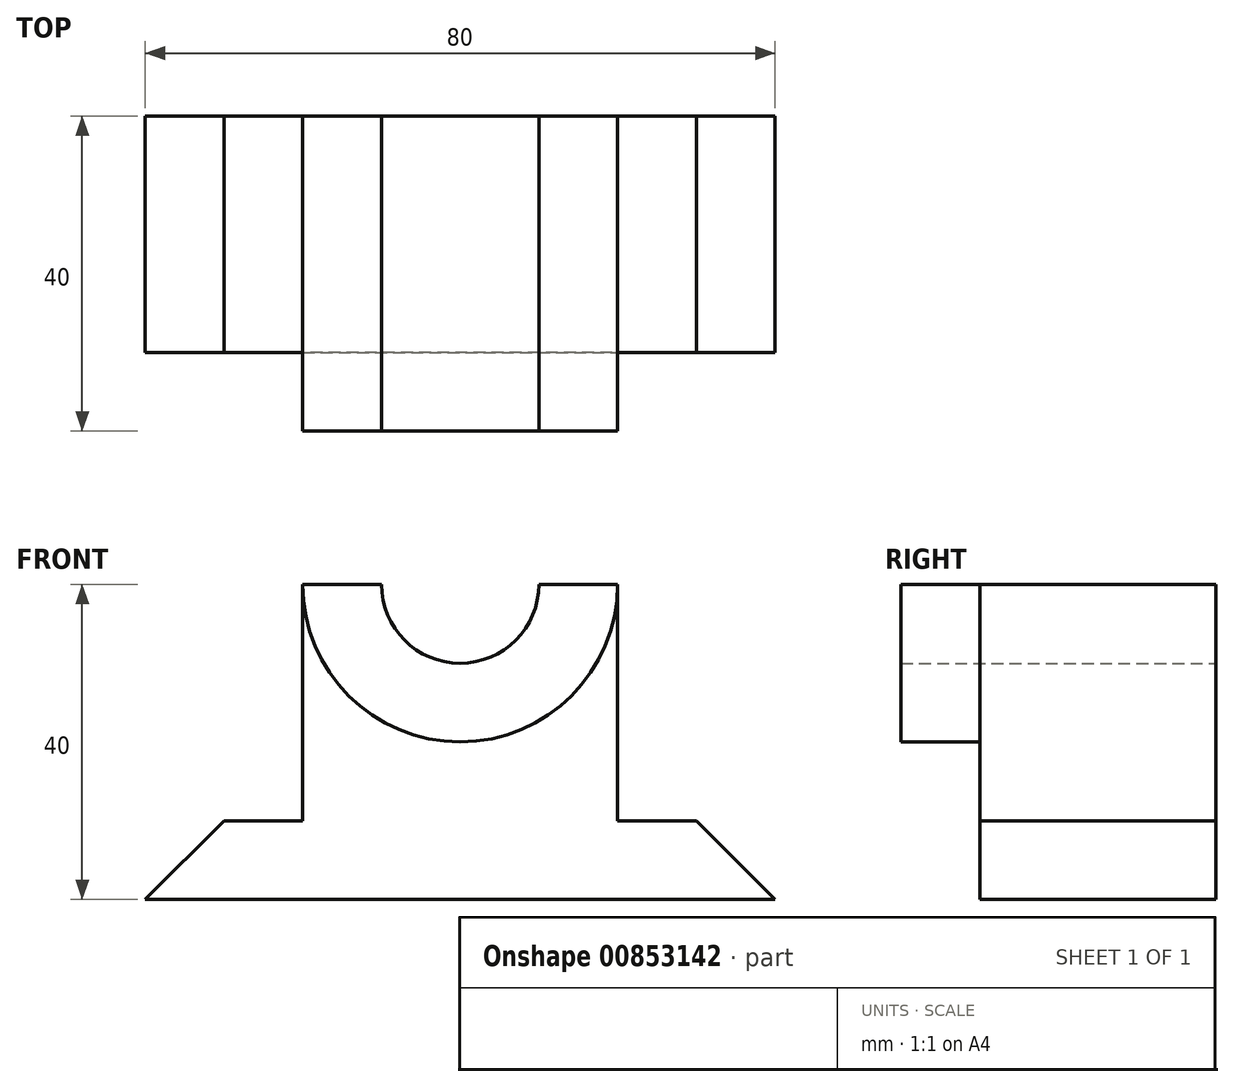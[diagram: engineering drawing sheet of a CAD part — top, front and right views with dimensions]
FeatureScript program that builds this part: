
annotation { "Feature Type Name" : "Feature", "Feature Type Description" : "" }
export const myFeature = defineFeature(function(context is Context, id is Id, definition is map)
    precondition{}
    {
        {
            var Q0;
            Q0=qCreatedBy(makeId("Front.planeOp"),FACE);
            var sketch = newSketch(context, id + "F0", { "sketchPlane" : qUnion([Q0])});
            skLineSegment(sketch, "E0", {"start": v(-40, 0) * mm, "end": v(-30, 10) * mm});
            skLineSegment(sketch, "E1", {"start": v(-30, 10) * mm, "end": v(-20, 10) * mm});
            skLineSegment(sketch, "E2", {"start": v(-20, 10) * mm, "end": v(-20, 40) * mm});
            skLineSegment(sketch, "E3", {"start": v(-20, 40) * mm, "end": v(-10, 40) * mm});
            skLineSegment(sketch, "E4", {"start": v(20, 40) * mm, "end": v(20, 10) * mm});
            skLineSegment(sketch, "E5", {"start": v(20, 10) * mm, "end": v(30, 10) * mm});
            skLineSegment(sketch, "E6", {"start": v(30, 10) * mm, "end": v(40, 0) * mm});
            skLineSegment(sketch, "E7", {"start": v(40, 0) * mm, "end": v(-40, 0) * mm});
            skArc(sketch, "E8", {"start": v(-10, 40) * mm, "mid": v(0, 30) * mm, "end": v(10, 40) * mm});
            skLineSegment(sketch, "E9.trimOffspring", {"start": v(10, 40) * mm, "end": v(20, 40) * mm});
            skSolve(sketch);
        }
        {
            var Q0;
            Q0 = qSketchRegion(id + "F0", true);
            extrude(context, id + "F1", {"entities" : qUnion([Q0]), "depth" : 30 * mm, "offsetDistance" : 25 * mm});
        }
        {
            var Q0;
            Q0=makeQuery(id+"F1.opExtrude","CAP_FACE",FACE,{"disambiguationData":[OSD([sQuery(id+"F0.wireOp",EDGE,"E0"),sQuery(id+"F0.wireOp",EDGE,"E1"),sQuery(id+"F0.wireOp",EDGE,"E2"),sQuery(id+"F0.wireOp",EDGE,"E3"),sQuery(id+"F0.wireOp",EDGE,"E4"),sQuery(id+"F0.wireOp",EDGE,"E5"),sQuery(id+"F0.wireOp",EDGE,"E6"),sQuery(id+"F0.wireOp",EDGE,"E7"),sQuery(id+"F0.wireOp",EDGE,"E8"),sQuery(id+"F0.wireOp",EDGE,"E9.trimOffspring")])],"isStart":false});
            var sketch = newSketch(context, id + "F2", { "sketchPlane" : qUnion([Q0])});
            skArc(sketch, "E10", {"start": v(-20, 40) * mm, "mid": v(0, 20) * mm, "end": v(20, 40) * mm});
            skArc(sketch, "E11", {"start": v(-10, 40) * mm, "mid": v(0, 30) * mm, "end": v(10, 40) * mm});
            skLineSegment(sketch, "E12", {"start": v(-20, 40) * mm, "end": v(-10, 40) * mm});
            skLineSegment(sketch, "E13.trimOffspring", {"start": v(10, 40) * mm, "end": v(20, 40) * mm});
            skSolve(sketch);
        }
        {
            var Q0;
            Q0 = qSketchRegion(id + "F2", true);
            extrude(context, id + "F3", {"entities" : qUnion([Q0]), "operationType" : NewBodyOperationType.ADD, "depth" : 10 * mm, "offsetDistance" : 25 * mm});
        }
    });
